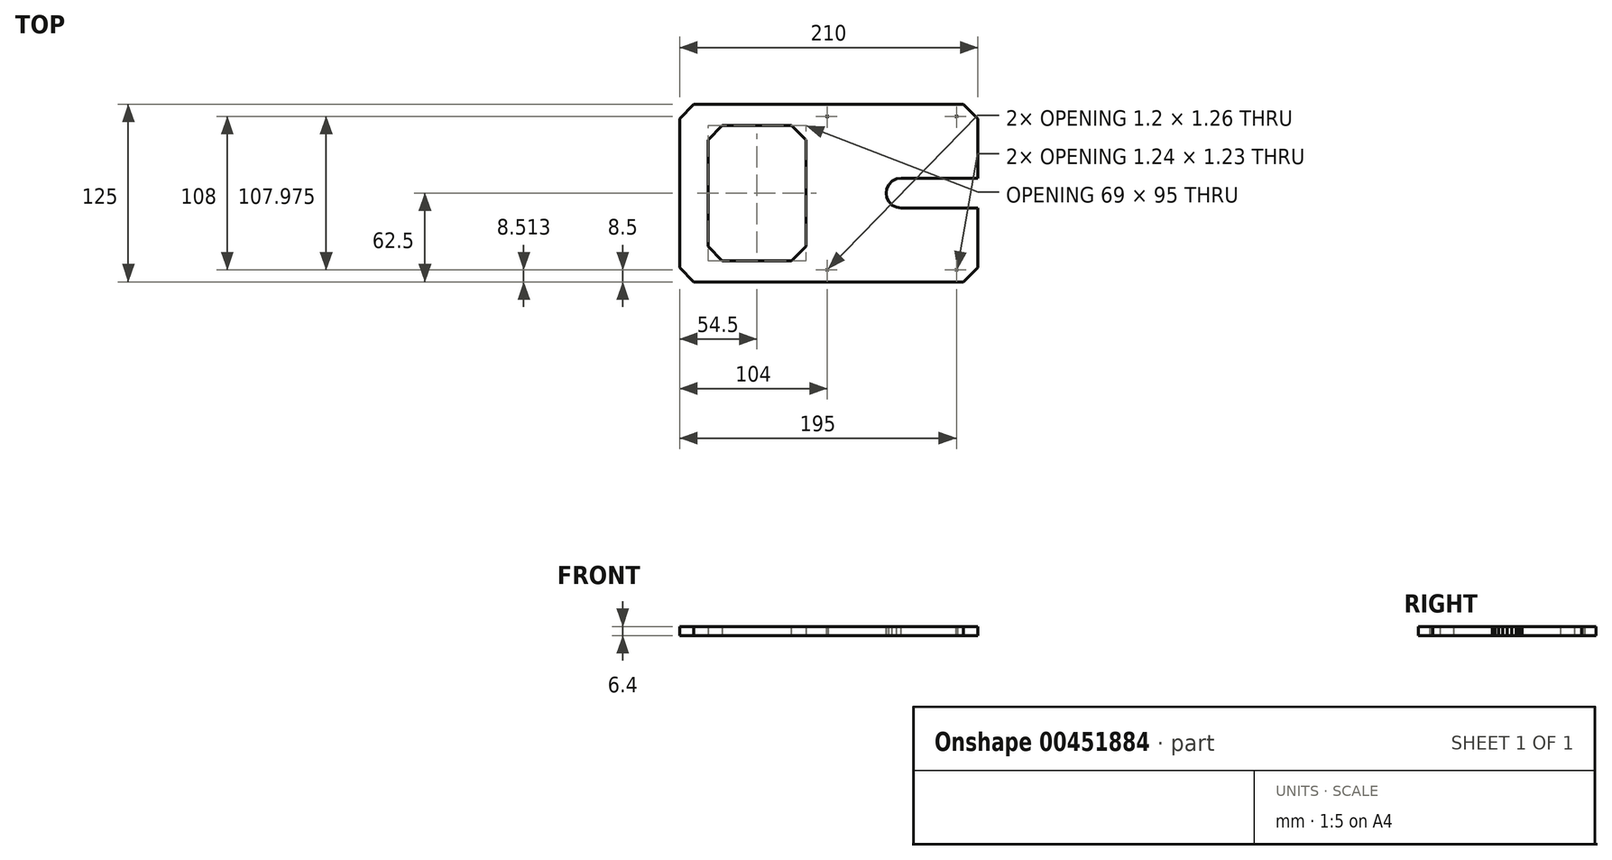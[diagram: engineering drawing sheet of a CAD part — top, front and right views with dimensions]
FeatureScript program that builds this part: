
annotation { "Feature Type Name" : "Feature", "Feature Type Description" : "" }
export const myFeature = defineFeature(function(context is Context, id is Id, definition is map)
    precondition{}
    {
        {
            var Q0;
            Q0=qCreatedBy(makeId("Top.planeOp"),FACE);
            var sketch = newSketch(context, id + "F0", { "sketchPlane" : qUnion([Q0])});
            skLineSegment(sketch, "E0.bottom", {"start": v(105, -62.5) * mm, "end": v(-105, -62.5) * mm});
            skLineSegment(sketch, "E0.top", {"start": v(105, 62.5) * mm, "end": v(-105, 62.5) * mm});
            skLineSegment(sketch, "E0.left", {"start": v(105, -62.5) * mm, "end": v(105, 62.5) * mm});
            skLineSegment(sketch, "E0.right", {"start": v(-105, -62.5) * mm, "end": v(-105, 62.5) * mm});
            skPoint(sketch, "E0.middle", {"position": v(0, 0) * mm});
            skLineSegment(sketch, "E1", {"start": v(-105, 0) * mm, "end": v(105, 0) * mm, "construction": true});
            skLineSegment(sketch, "E2", {"start": v(0, 62.5) * mm, "end": v(0, -62.5) * mm, "construction": true});
            skSolve(sketch);
        }
        {
            var Q0;
            Q0=makeQuery(id+"F0.imprint","IMPRINT",FACE,{"disambiguationData":[TD([[makeQuery(id+"F0.imprint","IMPRINT",EDGE,{"derivedFrom":sQuery(id+"F0.wireOp",EDGE,"E0.bottom")}),-1.0]])]});
            extrude(context, id + "F1", {"entities" : qUnion([Q0]), "depth" : 6.4 * mm});
        }
        {
            var Q0;
            Q0=makeQuery(id+"F1.opExtrude","CAP_FACE",FACE,{"disambiguationData":[OSD([sQuery(id+"F0.wireOp",EDGE,"E0.bottom"),sQuery(id+"F0.wireOp",EDGE,"E0.top"),sQuery(id+"F0.wireOp",EDGE,"E0.left"),sQuery(id+"F0.wireOp",EDGE,"E0.right")])],"isStart":false});
            var sketch = newSketch(context, id + "F2", { "sketchPlane" : qUnion([Q0])});
            skLineSegment(sketch, "E3", {"start": v(51, 10.5) * mm, "end": v(105, 10.5) * mm});
            skLineSegment(sketch, "E4.MirrorCS", {"start": v(51, -10.5) * mm, "end": v(105, -10.5) * mm});
            skLineSegment(sketch, "E5", {"start": v(90, 62.5) * mm, "end": v(90, -62.5) * mm, "construction": true});
            skLineSegment(sketch, "E6", {"start": v(105, 10.5) * mm, "end": v(105, -10.5) * mm});
            skCircle(sketch, "E7.cCircle", {"center": v(51, 0) * mm, "radius": 10.5 * mm, "construction": true});
            skLineSegment(sketch, "E7.0", {"start": v(51, 10.5) * mm, "end": v(54.24, 9.99) * mm, "construction": true});
            skLineSegment(sketch, "E7.1", {"start": v(54.24, 9.99) * mm, "end": v(57.17, 8.5) * mm, "construction": true});
            skLineSegment(sketch, "E7.2", {"start": v(57.17, 8.5) * mm, "end": v(59.5, 6.17) * mm, "construction": true});
            skLineSegment(sketch, "E7.3", {"start": v(59.5, 6.17) * mm, "end": v(60.99, 3.24) * mm, "construction": true});
            skLineSegment(sketch, "E7.4", {"start": v(60.99, 3.24) * mm, "end": v(61.5, 0) * mm, "construction": true});
            skLineSegment(sketch, "E7.5", {"start": v(61.5, 0) * mm, "end": v(60.99, -3.24) * mm, "construction": true});
            skLineSegment(sketch, "E7.6", {"start": v(60.99, -3.24) * mm, "end": v(59.5, -6.17) * mm, "construction": true});
            skLineSegment(sketch, "E7.7", {"start": v(59.5, -6.17) * mm, "end": v(57.17, -8.5) * mm, "construction": true});
            skLineSegment(sketch, "E7.8", {"start": v(57.17, -8.5) * mm, "end": v(54.24, -9.99) * mm, "construction": true});
            skLineSegment(sketch, "E7.9", {"start": v(54.24, -9.99) * mm, "end": v(51, -10.5) * mm, "construction": true});
            skLineSegment(sketch, "E7.10", {"start": v(51, -10.5) * mm, "end": v(47.76, -9.99) * mm});
            skLineSegment(sketch, "E7.11", {"start": v(47.76, -9.99) * mm, "end": v(44.83, -8.5) * mm});
            skLineSegment(sketch, "E7.12", {"start": v(44.83, -8.5) * mm, "end": v(42.5, -6.17) * mm});
            skLineSegment(sketch, "E7.13", {"start": v(42.5, -6.17) * mm, "end": v(41.01, -3.24) * mm});
            skLineSegment(sketch, "E7.14", {"start": v(41.01, -3.24) * mm, "end": v(40.5, 0) * mm});
            skLineSegment(sketch, "E7.15", {"start": v(40.5, 0) * mm, "end": v(41.01, 3.24) * mm});
            skLineSegment(sketch, "E7.16", {"start": v(41.01, 3.24) * mm, "end": v(42.5, 6.17) * mm});
            skLineSegment(sketch, "E7.17", {"start": v(42.5, 6.17) * mm, "end": v(44.83, 8.5) * mm});
            skLineSegment(sketch, "E7.18", {"start": v(44.83, 8.5) * mm, "end": v(47.76, 9.99) * mm});
            skLineSegment(sketch, "E7.19", {"start": v(47.76, 9.99) * mm, "end": v(51, 10.5) * mm});
            skSolve(sketch);
        }
        {
            var Q0;
            Q0 = qSketchRegion(id + "F2", true);
            extrude(context, id + "F3", {"entities" : qUnion([Q0]), "operationType" : NewBodyOperationType.REMOVE, "oppositeDirection" : true, "depth" : 25 * mm});
        }
        {
            var Q0;
            Q0=qCreatedBy(makeId("Top.planeOp"),FACE);
            var sketch = newSketch(context, id + "F4", { "sketchPlane" : qUnion([Q0])});
            skLineSegment(sketch, "E8.0", {"start": v(90, 62.5) * mm, "end": v(90, -62.5) * mm, "construction": true});
            skLineSegment(sketch, "E9", {"start": v(0, 0) * mm, "end": v(90, 0) * mm, "construction": true});
            skCircle(sketch, "E10.cCircle", {"center": v(90, 54) * mm, "radius": 0.6 * mm, "construction": true});
            skLineSegment(sketch, "E10.0", {"start": v(90, 53.37) * mm, "end": v(89.66, 53.47) * mm});
            skLineSegment(sketch, "E10.1", {"start": v(89.66, 53.47) * mm, "end": v(89.43, 53.74) * mm});
            skLineSegment(sketch, "E10.2", {"start": v(89.43, 53.74) * mm, "end": v(89.38, 54.09) * mm});
            skLineSegment(sketch, "E10.3", {"start": v(89.38, 54.09) * mm, "end": v(89.53, 54.4) * mm});
            skLineSegment(sketch, "E10.4", {"start": v(89.53, 54.4) * mm, "end": v(89.82, 54.6) * mm});
            skLineSegment(sketch, "E10.5", {"start": v(89.82, 54.6) * mm, "end": v(90.18, 54.6) * mm});
            skLineSegment(sketch, "E10.6", {"start": v(90.18, 54.6) * mm, "end": v(90.47, 54.4) * mm});
            skLineSegment(sketch, "E10.7", {"start": v(90.47, 54.4) * mm, "end": v(90.62, 54.09) * mm});
            skLineSegment(sketch, "E10.8", {"start": v(90.62, 54.09) * mm, "end": v(90.57, 53.74) * mm});
            skLineSegment(sketch, "E10.9", {"start": v(90.57, 53.74) * mm, "end": v(90.34, 53.47) * mm});
            skLineSegment(sketch, "E10.10", {"start": v(90.34, 53.47) * mm, "end": v(90, 53.37) * mm});
            skPoint(sketch, "E10.0.midPoint", {"position": v(89.83, 53.42) * mm});
            skCircle(sketch, "E11.MirrorC", {"center": v(90, -54) * mm, "radius": 0.6 * mm, "construction": true});
            skLineSegment(sketch, "E12.MirrorCS", {"start": v(90.62, -54.09) * mm, "end": v(90.57, -53.74) * mm});
            skLineSegment(sketch, "E13.MirrorCS", {"start": v(90.47, -54.4) * mm, "end": v(90.62, -54.09) * mm});
            skLineSegment(sketch, "E14.MirrorCS", {"start": v(90.18, -54.6) * mm, "end": v(90.47, -54.4) * mm});
            skLineSegment(sketch, "E15.MirrorCS", {"start": v(89.82, -54.6) * mm, "end": v(90.18, -54.6) * mm});
            skLineSegment(sketch, "E16.MirrorCS", {"start": v(89.53, -54.4) * mm, "end": v(89.82, -54.6) * mm});
            skLineSegment(sketch, "E17.MirrorCS", {"start": v(89.38, -54.09) * mm, "end": v(89.53, -54.4) * mm});
            skLineSegment(sketch, "E18.MirrorCS", {"start": v(89.43, -53.74) * mm, "end": v(89.38, -54.09) * mm});
            skLineSegment(sketch, "E19.MirrorCS", {"start": v(89.66, -53.47) * mm, "end": v(89.43, -53.74) * mm});
            skLineSegment(sketch, "E20.MirrorCS", {"start": v(90, -53.37) * mm, "end": v(89.66, -53.47) * mm});
            skLineSegment(sketch, "E21.MirrorCS", {"start": v(90.57, -53.74) * mm, "end": v(90.34, -53.47) * mm});
            skLineSegment(sketch, "E22.MirrorCS", {"start": v(90.34, -53.47) * mm, "end": v(90, -53.37) * mm});
            skPoint(sketch, "E23.MirrorP", {"position": v(89.83, -53.42) * mm});
            skLineSegment(sketch, "E24", {"start": v(-1, 62.5) * mm, "end": v(-1, -62.5) * mm, "construction": true});
            skCircle(sketch, "E25.cCircle", {"center": v(-1, 54) * mm, "radius": 0.6 * mm, "construction": true});
            skLineSegment(sketch, "E25.0", {"start": v(-0.4, 53.8) * mm, "end": v(-0.63, 53.49) * mm});
            skLineSegment(sketch, "E25.1", {"start": v(-0.63, 53.49) * mm, "end": v(-1, 53.37) * mm});
            skLineSegment(sketch, "E25.2", {"start": v(-1, 53.37) * mm, "end": v(-1.37, 53.49) * mm});
            skLineSegment(sketch, "E25.3", {"start": v(-1.37, 53.49) * mm, "end": v(-1.6, 53.8) * mm});
            skLineSegment(sketch, "E25.4", {"start": v(-1.6, 53.8) * mm, "end": v(-1.6, 54.2) * mm});
            skLineSegment(sketch, "E25.5", {"start": v(-1.6, 54.2) * mm, "end": v(-1.37, 54.51) * mm});
            skLineSegment(sketch, "E25.6", {"start": v(-1.37, 54.51) * mm, "end": v(-1, 54.63) * mm});
            skLineSegment(sketch, "E25.7", {"start": v(-1, 54.63) * mm, "end": v(-0.63, 54.51) * mm});
            skLineSegment(sketch, "E25.8", {"start": v(-0.63, 54.51) * mm, "end": v(-0.4, 54.2) * mm});
            skLineSegment(sketch, "E25.9", {"start": v(-0.4, 54.2) * mm, "end": v(-0.4, 53.8) * mm});
            skPoint(sketch, "E25.0.midPoint", {"position": v(-0.51, 53.65) * mm});
            skLineSegment(sketch, "E26.MirrorCS", {"start": v(-1.6, -53.8) * mm, "end": v(-1.6, -54.2) * mm});
            skLineSegment(sketch, "E27.MirrorCS", {"start": v(-0.63, -53.49) * mm, "end": v(-1, -53.37) * mm});
            skLineSegment(sketch, "E28.MirrorCS", {"start": v(-1, -54.63) * mm, "end": v(-0.63, -54.51) * mm});
            skLineSegment(sketch, "E29.MirrorCS", {"start": v(-0.4, -53.8) * mm, "end": v(-0.63, -53.49) * mm});
            skLineSegment(sketch, "E30.MirrorCS", {"start": v(-0.4, -54.2) * mm, "end": v(-0.4, -53.8) * mm});
            skLineSegment(sketch, "E31.MirrorCS", {"start": v(-1.6, -54.2) * mm, "end": v(-1.37, -54.51) * mm});
            skLineSegment(sketch, "E32.MirrorCS", {"start": v(-1.37, -54.51) * mm, "end": v(-1, -54.63) * mm});
            skLineSegment(sketch, "E33.MirrorCS", {"start": v(-1.37, -53.49) * mm, "end": v(-1.6, -53.8) * mm});
            skLineSegment(sketch, "E34.MirrorCS", {"start": v(-1, -53.37) * mm, "end": v(-1.37, -53.49) * mm});
            skLineSegment(sketch, "E35.MirrorCS", {"start": v(-0.63, -54.51) * mm, "end": v(-0.4, -54.2) * mm});
            skCircle(sketch, "E36.MirrorC", {"center": v(-1, -54) * mm, "radius": 0.6 * mm, "construction": true});
            skPoint(sketch, "E37.MirrorP", {"position": v(-0.51, -53.65) * mm});
            skSolve(sketch);
        }
        {
            var Q0;
            Q0 = qSketchRegion(id + "F4", true);
            extrude(context, id + "F5", {"entities" : qUnion([Q0]), "operationType" : NewBodyOperationType.REMOVE, "endBound" : BoundingType.THROUGH_ALL, "depth" : 25 * mm});
        }
        {
            var Q0;
            Q0=makeQuery(id+"F1.opExtrude","SWEPT_EDGE",EDGE,{"disambiguationData":[OSD([sQuery(id+"F0.wireOp",EDGE,"E0.top"),sQuery(id+"F0.wireOp",EDGE,"E0.right")])]});
            var Q1;
            Q1=makeQuery(id+"F1.opExtrude","SWEPT_EDGE",EDGE,{"disambiguationData":[OSD([sQuery(id+"F0.wireOp",EDGE,"E0.top"),sQuery(id+"F0.wireOp",EDGE,"E0.left")])]});
            var Q2;
            Q2=makeQuery(id+"F1.opExtrude","SWEPT_EDGE",EDGE,{"disambiguationData":[OSD([sQuery(id+"F0.wireOp",EDGE,"E0.bottom"),sQuery(id+"F0.wireOp",EDGE,"E0.left")])]});
            var Q3;
            Q3=makeQuery(id+"F1.opExtrude","SWEPT_EDGE",EDGE,{"disambiguationData":[OSD([sQuery(id+"F0.wireOp",EDGE,"E0.bottom"),sQuery(id+"F0.wireOp",EDGE,"E0.right")])]});
            chamfer(context, id + "F6", {"entities" : qUnion([Q0, Q1, Q2, Q3]), "width" : 10 * mm, "tangentPropagation" : true});
        }
        {
            var Q0;
            Q0=makeQuery(id+"F1.opExtrude","CAP_FACE",FACE,{"disambiguationData":[OSD([sQuery(id+"F0.wireOp",EDGE,"E0.bottom"),sQuery(id+"F0.wireOp",EDGE,"E0.top"),sQuery(id+"F0.wireOp",EDGE,"E0.left"),sQuery(id+"F0.wireOp",EDGE,"E0.right")])],"isStart":true});
            var sketch = newSketch(context, id + "F7", { "sketchPlane" : qUnion([Q0])});
            skLineSegment(sketch, "E38.bottom", {"start": v(-16, -47.5) * mm, "end": v(-85, -47.5) * mm});
            skLineSegment(sketch, "E38.top", {"start": v(-16, 47.5) * mm, "end": v(-85, 47.5) * mm});
            skLineSegment(sketch, "E38.left", {"start": v(-16, -47.5) * mm, "end": v(-16, 47.5) * mm});
            skLineSegment(sketch, "E38.right", {"start": v(-85, -47.5) * mm, "end": v(-85, 47.5) * mm});
            skPoint(sketch, "E38.middle", {"position": v(-50.5, 0) * mm});
            skSolve(sketch);
        }
        {
            var Q0;
            Q0=makeQuery(id+"F7.imprint","IMPRINT",FACE,{"disambiguationData":[TD([[makeQuery(id+"F7.imprint","IMPRINT",EDGE,{"derivedFrom":sQuery(id+"F7.wireOp",EDGE,"E38.bottom")}),-1.0]])]});
            extrude(context, id + "F8", {"entities" : qUnion([Q0]), "operationType" : NewBodyOperationType.REMOVE, "endBound" : BoundingType.THROUGH_ALL, "oppositeDirection" : true, "depth" : 25 * mm});
        }
        {
            var Q0;
            Q0=makeQuery(id+"F8.boolean.opBoolean","COPY",EDGE,{"derivedFrom":makeQuery(id+"F8.opExtrude","SWEPT_EDGE",EDGE,{"disambiguationData":[OSD([sQuery(id+"F7.wireOp",EDGE,"E38.bottom"),sQuery(id+"F7.wireOp",EDGE,"E38.right")])]})});
            var Q1;
            Q1=makeQuery(id+"F8.boolean.opBoolean","COPY",EDGE,{"derivedFrom":makeQuery(id+"F8.opExtrude","SWEPT_EDGE",EDGE,{"disambiguationData":[OSD([sQuery(id+"F7.wireOp",EDGE,"E38.bottom"),sQuery(id+"F7.wireOp",EDGE,"E38.left")])]})});
            var Q2;
            Q2=makeQuery(id+"F8.boolean.opBoolean","COPY",EDGE,{"derivedFrom":makeQuery(id+"F8.opExtrude","SWEPT_EDGE",EDGE,{"disambiguationData":[OSD([sQuery(id+"F7.wireOp",EDGE,"E38.top"),sQuery(id+"F7.wireOp",EDGE,"E38.left")])]})});
            var Q3;
            Q3=makeQuery(id+"F8.boolean.opBoolean","COPY",EDGE,{"derivedFrom":makeQuery(id+"F8.opExtrude","SWEPT_EDGE",EDGE,{"disambiguationData":[OSD([sQuery(id+"F7.wireOp",EDGE,"E38.top"),sQuery(id+"F7.wireOp",EDGE,"E38.right")])]})});
            chamfer(context, id + "F9", {"entities" : qUnion([Q0, Q1, Q2, Q3]), "width" : 10 * mm, "tangentPropagation" : true});
        }
    });
